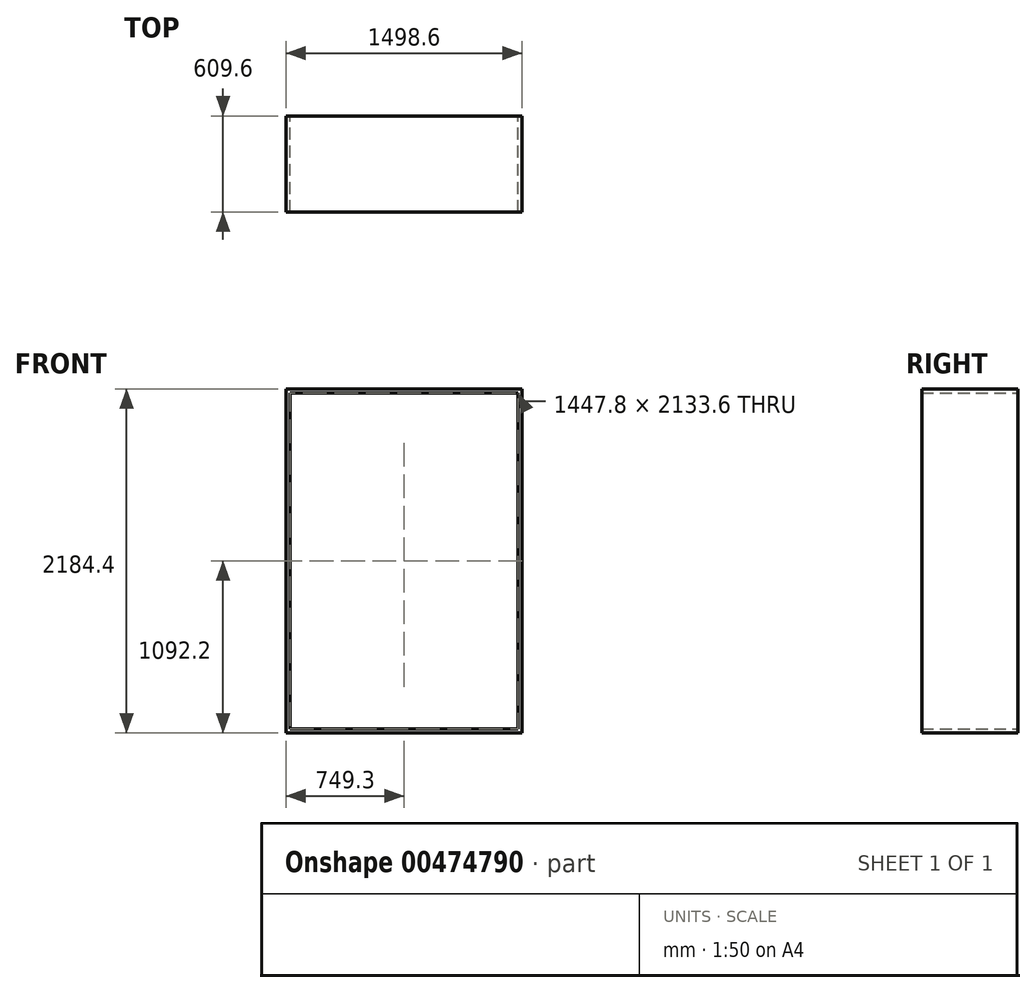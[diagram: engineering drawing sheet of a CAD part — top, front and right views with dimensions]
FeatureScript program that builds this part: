
annotation { "Feature Type Name" : "Feature", "Feature Type Description" : "" }
export const myFeature = defineFeature(function(context is Context, id is Id, definition is map)
    precondition{}
    {
        {
            var Q0;
            Q0=qCreatedBy(makeId("Front.planeOp"),FACE);
            var sketch = newSketch(context, id + "F0", { "sketchPlane" : qUnion([Q0])});
            skLineSegment(sketch, "E0.bottom", {"start": v(-723.9, 1066.8) * mm, "end": v(723.9, 1066.8) * mm});
            skLineSegment(sketch, "E0.top", {"start": v(-723.9, -1066.8) * mm, "end": v(723.9, -1066.8) * mm});
            skLineSegment(sketch, "E0.left", {"start": v(-723.9, 1066.8) * mm, "end": v(-723.9, -1066.8) * mm});
            skLineSegment(sketch, "E0.right", {"start": v(723.9, 1066.8) * mm, "end": v(723.9, -1066.8) * mm});
            skLineSegment(sketch, "E1.0", {"start": v(-749.3, 1092.2) * mm, "end": v(-749.3, -1092.2) * mm});
            skLineSegment(sketch, "E1.1", {"start": v(-749.3, 1092.2) * mm, "end": v(749.3, 1092.2) * mm});
            skLineSegment(sketch, "E1.2", {"start": v(749.3, 1092.2) * mm, "end": v(749.3, -1092.2) * mm});
            skLineSegment(sketch, "E1.3", {"start": v(-749.3, -1092.2) * mm, "end": v(749.3, -1092.2) * mm});
            skSolve(sketch);
        }
        {
            var Q0;
            Q0=makeQuery(id+"F0.imprint","IMPRINT",FACE,{"disambiguationData":[TD([[makeQuery(id+"F0.imprint","IMPRINT",EDGE,{"derivedFrom":sQuery(id+"F0.wireOp",EDGE,"E0.bottom")}),1.0]])]});
            extrude(context, id + "F1", {"entities" : qUnion([Q0]), "depth" : 609.6 * mm});
        }
    });
